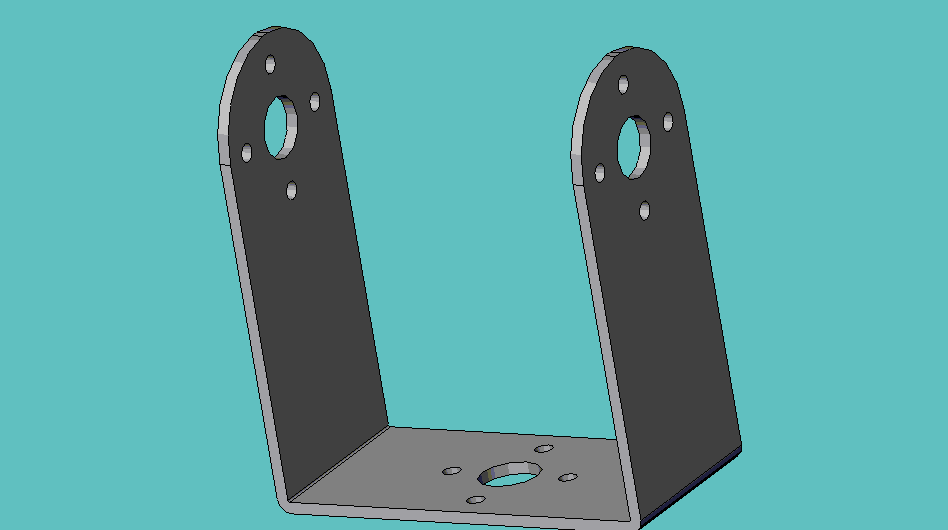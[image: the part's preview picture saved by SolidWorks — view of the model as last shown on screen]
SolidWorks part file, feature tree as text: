
SOLIDWORKS PART (.sldprt)
format: sldprt  version: not decoded by parser v0  size: 281,600 bytes
history: native  units: mm
features: sketch x3, extrude x2, fillet x2, material x1, cut_extrude x1 (+12 scaffold rows collapsed)
feature tree (21):
  scaffold x12  (default folders/planes/origin — collapsed)
  material  "Material <not specified>"
  sketch  "Sketch1"  dims[D1=0.06mm]
  extrude  "Extrude1"  Depth=1.524mm
  extrude  "Extrude2"  [1 undecoded]
  sketch  "Sketch1<3>"  dims[D1=58.3438mm]
  sketch  "Sketch4"  dims[D1=46.0502mm]
  cut_extrude  "Cut-Extrude1"  Depth=40.8686mm
  fillet  "Fillet1"  Radius=0.254mm
  fillet  "Fillet2"  Radius=1.778mm
decode coverage: 7 of 8 modeling features carry decoded parameters
note: 1 parameter value undecoded
note: suppression state not decoded; provenance and decode notes live in map.json
